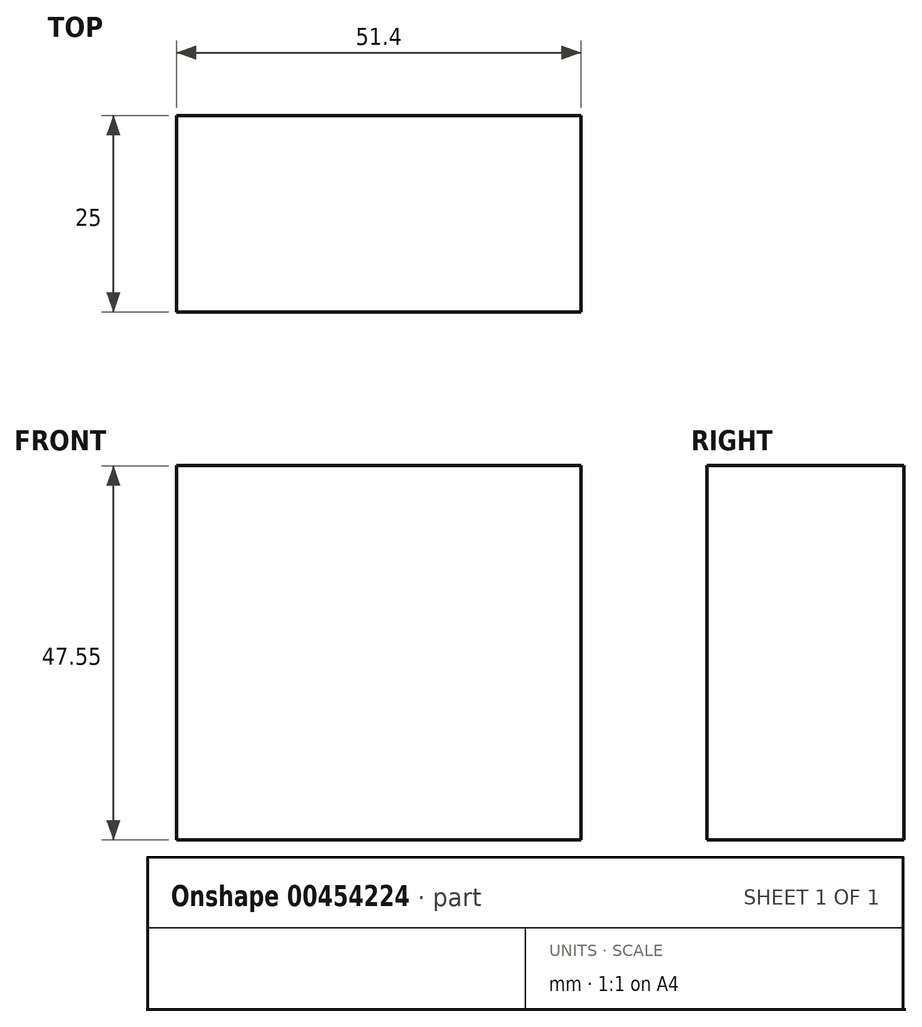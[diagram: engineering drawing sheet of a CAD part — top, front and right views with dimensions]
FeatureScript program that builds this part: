
annotation { "Feature Type Name" : "Feature", "Feature Type Description" : "" }
export const myFeature = defineFeature(function(context is Context, id is Id, definition is map)
    precondition{}
    {
        {
            var Q0;
            Q0=qCreatedBy(makeId("Front.planeOp"),FACE);
            var sketch = newSketch(context, id + "F0", { "sketchPlane" : qUnion([Q0])});
            skLineSegment(sketch, "E0.bottom", {"start": v(-91.8, 11.55) * mm, "end": v(-40.39, 11.55) * mm});
            skLineSegment(sketch, "E0.top", {"start": v(-91.8, 59.1) * mm, "end": v(-40.39, 59.1) * mm});
            skLineSegment(sketch, "E0.left", {"start": v(-91.8, 11.55) * mm, "end": v(-91.8, 59.1) * mm});
            skLineSegment(sketch, "E0.right", {"start": v(-40.39, 11.55) * mm, "end": v(-40.39, 59.1) * mm});
            skPoint(sketch, "E0.middle", {"position": v(-66.09, 35.33) * mm});
            skSolve(sketch);
        }
        {
            var Q0;
            Q0=makeQuery(id+"F0.imprint","IMPRINT",FACE,{"disambiguationData":[TD([[makeQuery(id+"F0.imprint","IMPRINT",EDGE,{"derivedFrom":sQuery(id+"F0.wireOp",EDGE,"E0.bottom")}),1.0]])]});
            extrude(context, id + "F1", {"entities" : qUnion([Q0]), "depth" : 25 * mm});
        }
    });
